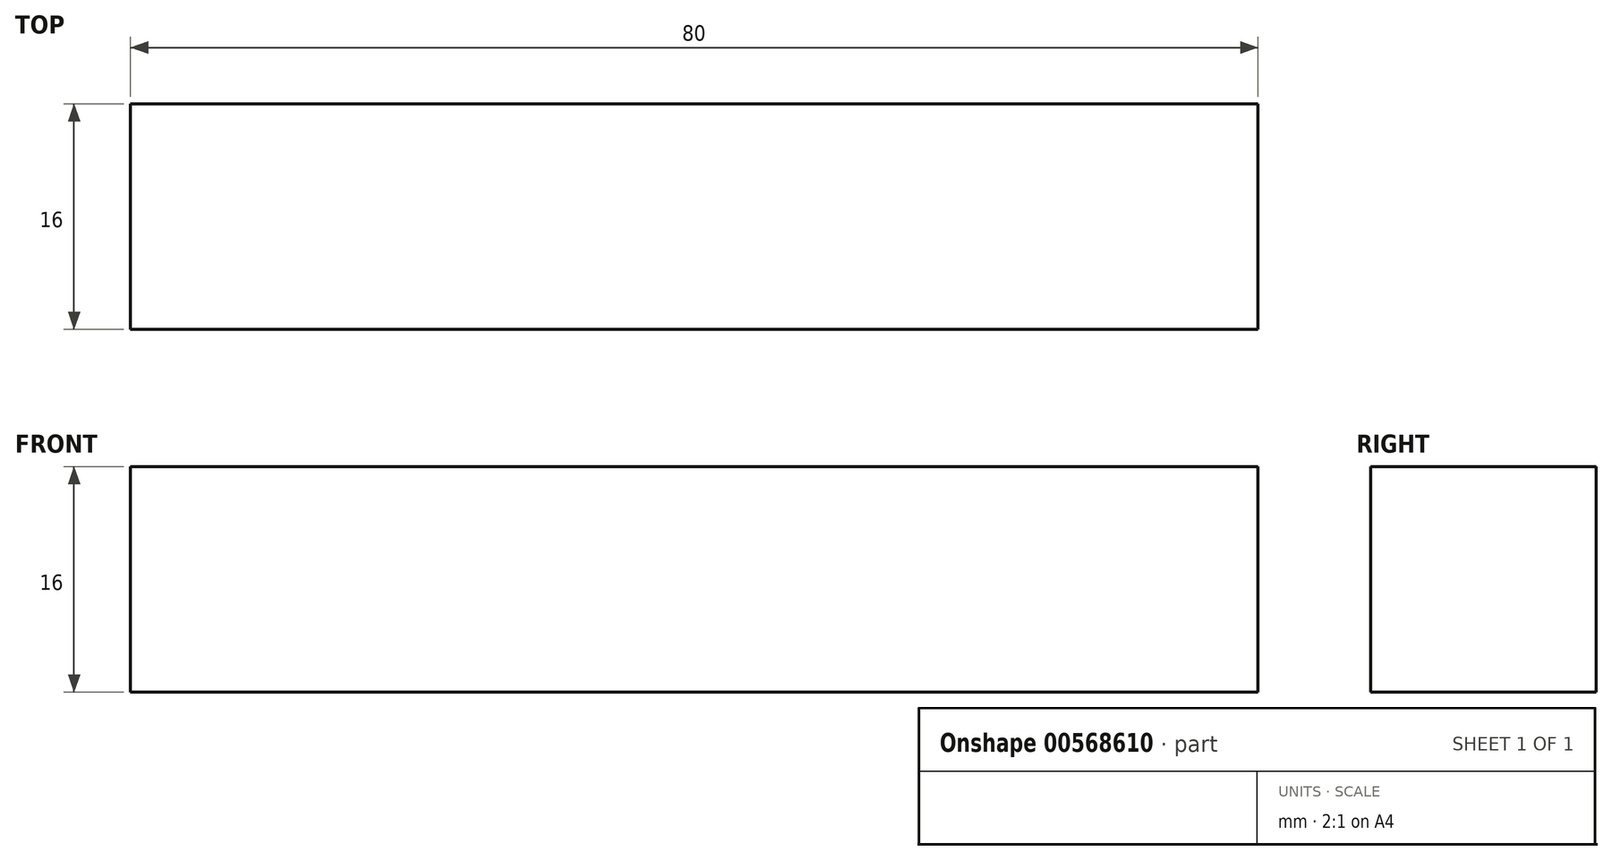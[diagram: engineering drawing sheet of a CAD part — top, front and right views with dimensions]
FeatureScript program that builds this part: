
annotation { "Feature Type Name" : "Feature", "Feature Type Description" : "" }
export const myFeature = defineFeature(function(context is Context, id is Id, definition is map)
    precondition{}
    {
        {
            var Q0;
            Q0=qCreatedBy(makeId("Top.planeOp"),FACE);
            var sketch = newSketch(context, id + "F0", { "sketchPlane" : qUnion([Q0])});
            skLineSegment(sketch, "E0.bottom", {"start": v(0, 0) * mm, "end": v(80, 0) * mm});
            skLineSegment(sketch, "E0.top", {"start": v(0, -16) * mm, "end": v(80, -16) * mm});
            skLineSegment(sketch, "E0.left", {"start": v(0, 0) * mm, "end": v(0, -16) * mm});
            skLineSegment(sketch, "E0.right", {"start": v(80, 0) * mm, "end": v(80, -16) * mm});
            skSolve(sketch);
        }
        {
            var Q0;
            Q0=makeQuery(id+"F0.imprint","IMPRINT",FACE,{"disambiguationData":[TD([[makeQuery(id+"F0.imprint","IMPRINT",EDGE,{"derivedFrom":sQuery(id+"F0.wireOp",EDGE,"E0.bottom")}),-1.0]])]});
            extrude(context, id + "F1", {"entities" : qUnion([Q0]), "depth" : 16 * mm, "offsetDistance" : 25 * mm});
        }
    });
